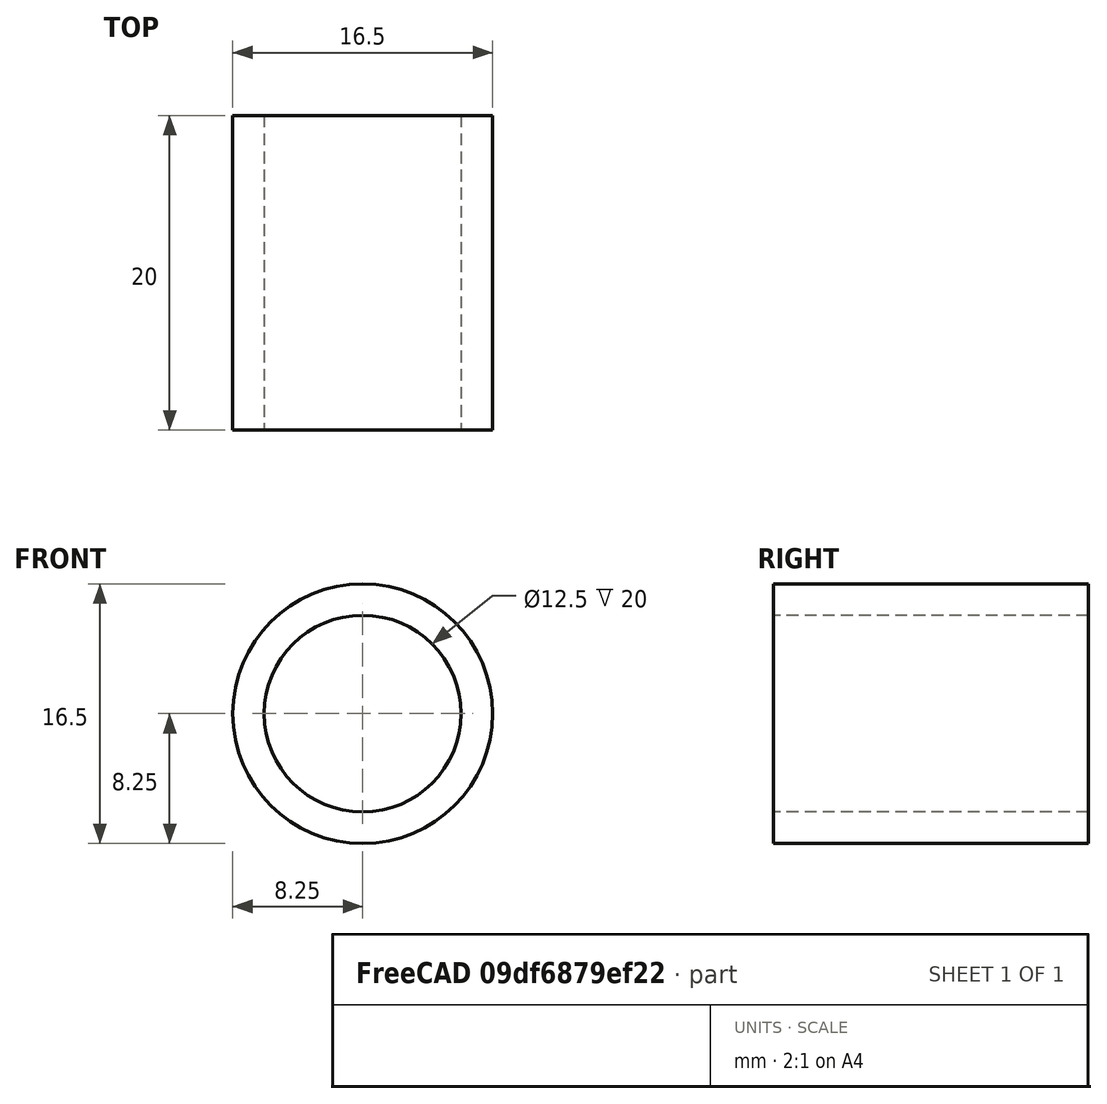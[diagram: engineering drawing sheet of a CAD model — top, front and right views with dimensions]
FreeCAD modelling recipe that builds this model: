
FCSTD DOCUMENT
Label: FilamentGuide
objects: Sketcher::SketchObject×1, PartDesign::Revolution×1
note: 2 computed .brp shape members not serialized (recipe doc carries the construction recipe); baked Part::Feature solids carry a one-line shape summary decoded from their .brp

FEATURE [Sketcher::SketchObject] Sketch
  sketch-geometry (6):
    g0: LineSegment StartX=6.25 StartY=20 StartZ=0 EndX=6.25 EndY=0 EndZ=0
    g1: LineSegment StartX=6.25 StartY=0 StartZ=0 EndX=8.25 EndY=0 EndZ=0
    g2: LineSegment StartX=8.25 StartY=0 StartZ=0 EndX=8.25 EndY=20 EndZ=0
    g3: ArcOfCircle CenterX=0.0139965 CenterY=20.418 CenterZ=0 NormalX=0 NormalY=0 NormalZ=1 Radius=6.25 StartAngle=6.21625 EndAngle=7.85622
    g4: ArcOfCircle CenterX=0.0139965 CenterY=20.418 CenterZ=0 NormalX=0 NormalY=0 NormalZ=1 Radius=8.24661 StartAngle=6.23247 EndAngle=7.85568
    g5: LineSegment StartX=0 StartY=28.6646 StartZ=0 EndX=0 EndY=26.668 EndZ=0
  constraints (19):
    c: Vertical(g0)
    c: Coincident(g0,g1)
    c: Horizontal(g1)
    c: Coincident(g1,g2)
    c: Vertical(g2)
    c: DistanceX(g0) = 6.25
    c: DistanceY(g0) = 0
    c: Distance(g1) = 2
    c: Equal(g2,g0)
    c: Distance(g2) = 20
    c: Coincident(g3,g0)
    c: Coincident(g4,g2)
    c: Coincident(g3,g4)
    c: Radius(g3) = 6.25
    c: Vertical(g5)
    c: Coincident(g4,g5)
    c: Coincident(g3,g5)
    c: Distance(g5) = 1.99661
    c: DistanceX(g3) = 0
FEATURE [PartDesign::Revolution] Revolution
  Angle = 360
  Axis = (0,1,0)
  Base = (0,0,0)
  Sketch = -> Sketch
